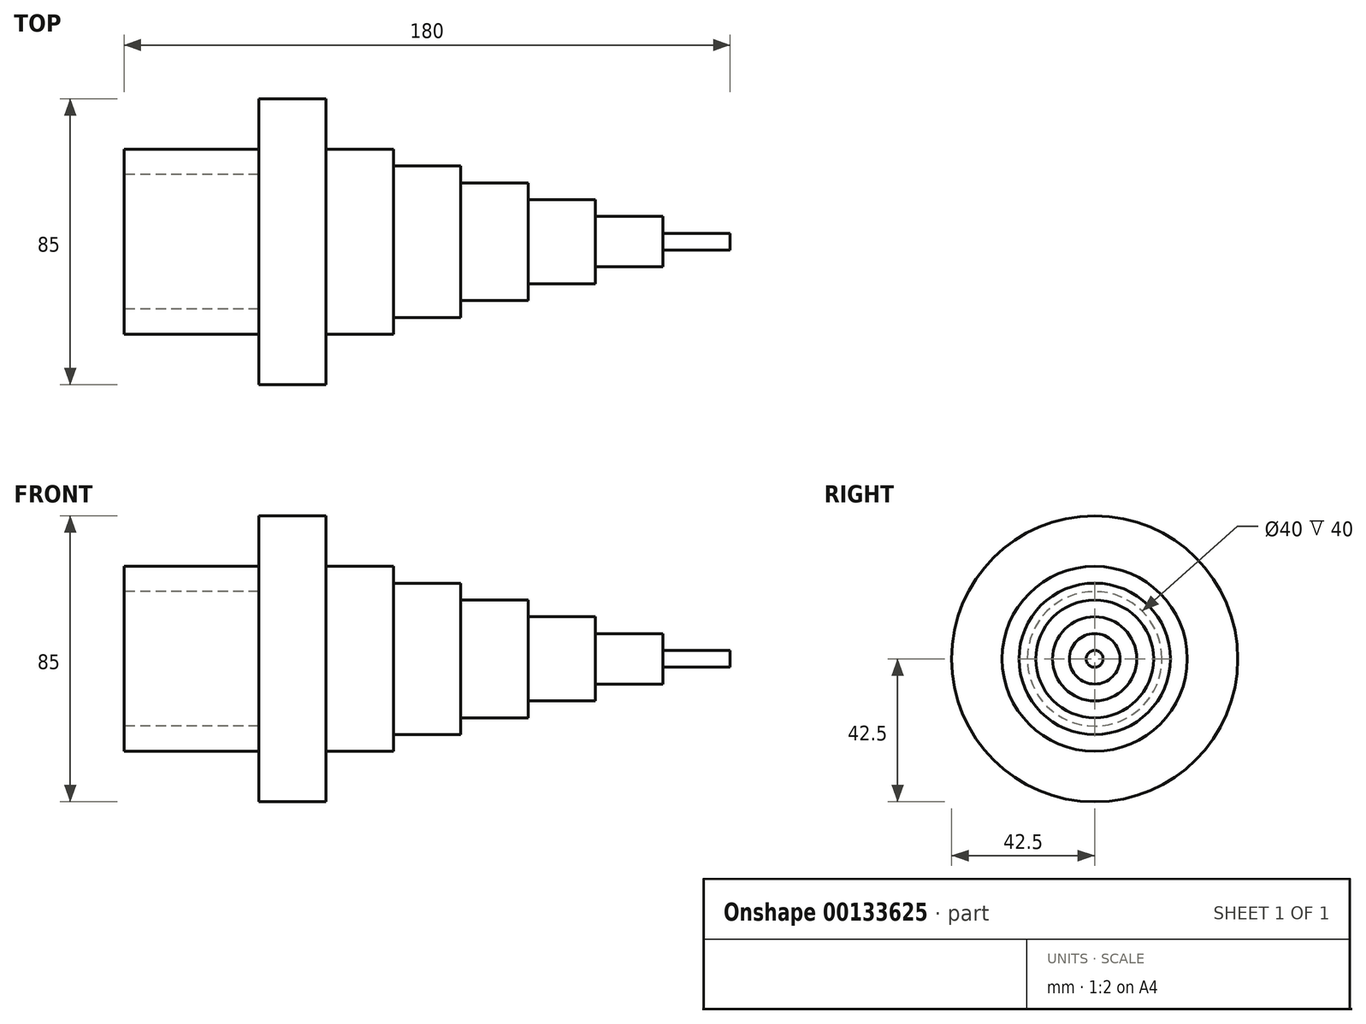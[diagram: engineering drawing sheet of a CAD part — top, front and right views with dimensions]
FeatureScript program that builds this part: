
annotation { "Feature Type Name" : "Feature", "Feature Type Description" : "" }
export const myFeature = defineFeature(function(context is Context, id is Id, definition is map)
    precondition{}
    {
        {
            var Q0;
            Q0=qCreatedBy(makeId("Front.planeOp"),FACE);
            var sketch = newSketch(context, id + "F0", { "sketchPlane" : qUnion([Q0])});
            skLineSegment(sketch, "E0", {"start": v(0, 0) * mm, "end": v(180, 0) * mm});
            skLineSegment(sketch, "E1", {"start": v(180, 0) * mm, "end": v(180, 2.5) * mm});
            skLineSegment(sketch, "E2", {"start": v(180, 2.5) * mm, "end": v(160, 2.5) * mm});
            skLineSegment(sketch, "E3", {"start": v(160, 2.5) * mm, "end": v(160, 7.5) * mm});
            skLineSegment(sketch, "E4", {"start": v(160, 7.5) * mm, "end": v(140, 7.5) * mm});
            skLineSegment(sketch, "E5", {"start": v(140, 7.5) * mm, "end": v(140, 12.5) * mm});
            skLineSegment(sketch, "E6", {"start": v(140, 12.5) * mm, "end": v(120, 12.5) * mm});
            skLineSegment(sketch, "E7", {"start": v(120, 12.5) * mm, "end": v(120, 17.5) * mm});
            skLineSegment(sketch, "E8", {"start": v(120, 17.5) * mm, "end": v(100, 17.5) * mm});
            skLineSegment(sketch, "E9", {"start": v(100, 17.5) * mm, "end": v(100, 22.5) * mm});
            skLineSegment(sketch, "E10", {"start": v(100, 22.5) * mm, "end": v(80, 22.5) * mm});
            skLineSegment(sketch, "E11", {"start": v(80, 22.5) * mm, "end": v(80, 27.5) * mm});
            skLineSegment(sketch, "E12", {"start": v(80, 27.5) * mm, "end": v(60, 27.5) * mm});
            skLineSegment(sketch, "E13", {"start": v(60, 27.5) * mm, "end": v(60, 42.5) * mm});
            skLineSegment(sketch, "E14", {"start": v(60, 42.5) * mm, "end": v(40, 42.5) * mm});
            skLineSegment(sketch, "E15", {"start": v(40, 42.5) * mm, "end": v(40, 27.5) * mm});
            skLineSegment(sketch, "E16", {"start": v(40, 27.5) * mm, "end": v(0, 27.5) * mm});
            skLineSegment(sketch, "E17", {"start": v(0, 27.5) * mm, "end": v(0, 0) * mm});
            skSolve(sketch);
        }
        {
            var Q0;
            Q0 = qSketchRegion(id + "F0", true);
            var Q1;
            Q1=sQuery(id+"F0.wireOp",EDGE,"E0");
            revolve(context, id + "F1", {"entities" : qUnion([Q0]), "axis" : qUnion([Q1]), "revolveType" : RevolveType.FULL});
        }
        {
            var Q0;
            Q0=makeQuery(id+"F1.opRevolve","SWEPT_FACE",FACE,{"disambiguationData":[OSD([sQuery(id+"F0.wireOp",EDGE,"E17")])]});
            var sketch = newSketch(context, id + "F2", { "sketchPlane" : qUnion([Q0])});
            skCircle(sketch, "E18", {"center": v(0, 0) * mm, "radius": 20 * mm});
            skSolve(sketch);
        }
        {
            var Q0;
            Q0 = qSketchRegion(id + "F2", true);
            extrude(context, id + "F3", {"entities" : qUnion([Q0]), "operationType" : NewBodyOperationType.REMOVE, "oppositeDirection" : true, "depth" : 40 * mm, "offsetDistance" : 25 * mm});
        }
    });
